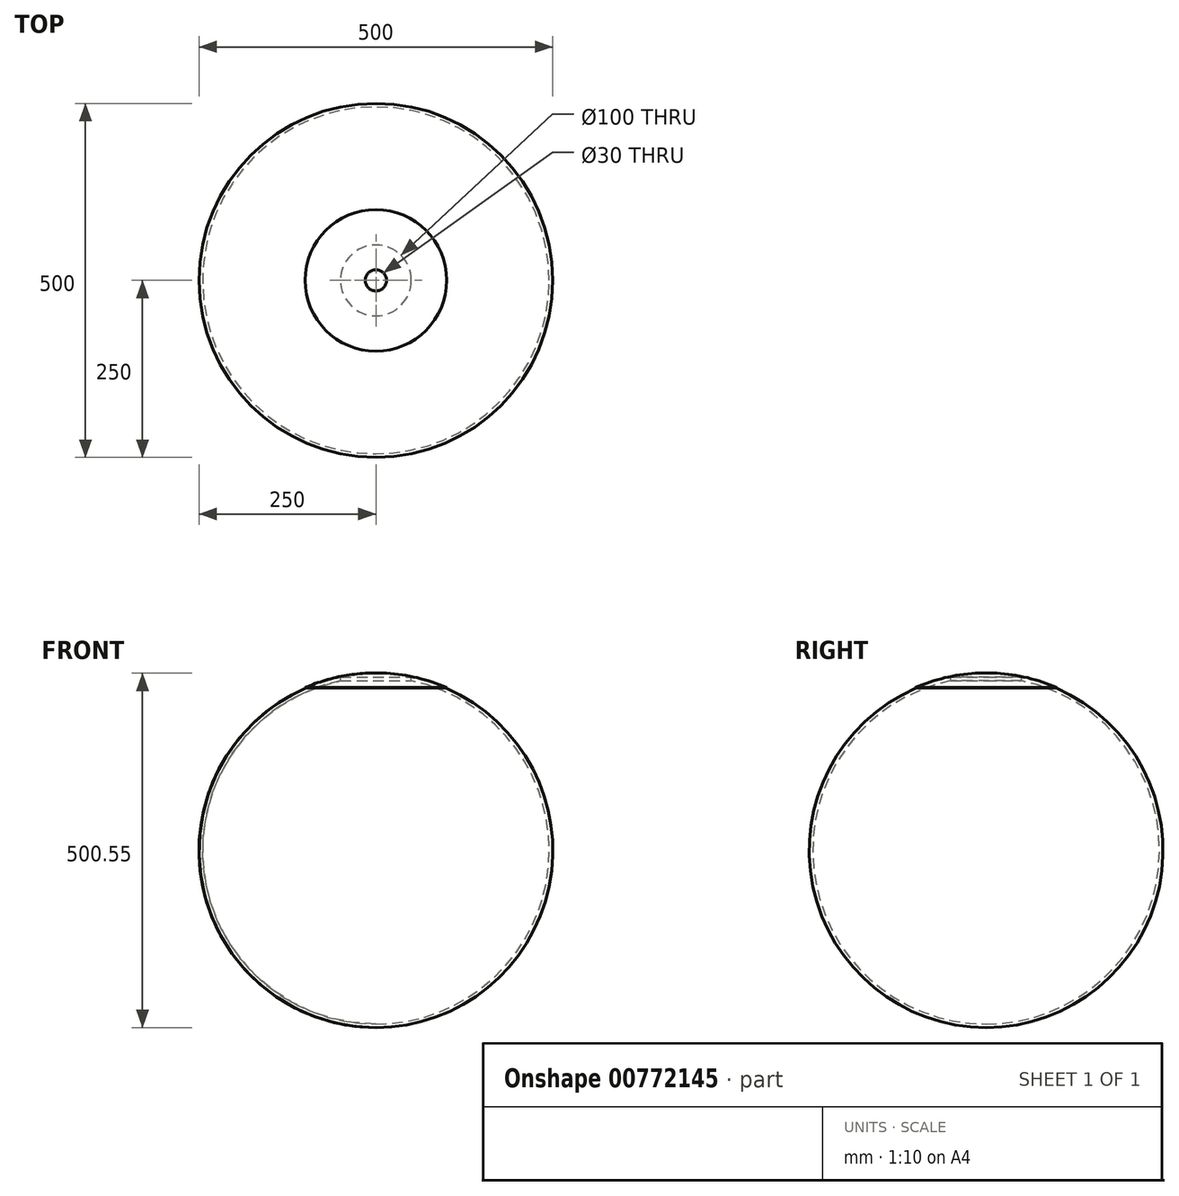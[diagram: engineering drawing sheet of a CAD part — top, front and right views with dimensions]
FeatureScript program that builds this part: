
annotation { "Feature Type Name" : "Feature", "Feature Type Description" : "" }
export const myFeature = defineFeature(function(context is Context, id is Id, definition is map)
    precondition{}
    {
        {
            var Q0;
            Q0=qCreatedBy(makeId("Front.planeOp"),FACE);
            var sketch = newSketch(context, id + "F0", { "sketchPlane" : qUnion([Q0])});
            skArc(sketch, "E0", {"start": v(0, -250) * mm, "mid": v(250, 0) * mm, "end": v(0, 250) * mm});
            skLineSegment(sketch, "E1", {"start": v(0, 269.53) * mm, "end": v(0, 245) * mm});
            skArc(sketch, "E2", {"start": v(0, -245) * mm, "mid": v(245, 0) * mm, "end": v(0, 245) * mm});
            skLineSegment(sketch, "E3.trimOffspring", {"start": v(0, -245) * mm, "end": v(0, -273.85) * mm});
            skSolve(sketch);
        }
        {
            var Q0;
            {var subQ0=sQuery(id+"F0.wireOp",EDGE,"E0");Q0=makeQuery(id+"F0.imprint","IMPRINT",FACE,{"disambiguationData":[TD([[makeQuery(id+"F0.imprint","IMPRINT",EDGE,{"derivedFrom":subQ0}),1.0]])]});}
            var Q1;
            Q1=sQuery(id+"F0.wireOp",EDGE,"E1");
            revolve(context, id + "F1", {"surfaceOperationType" : NewSurfaceOperationType.NEW, "entities" : qUnion([Q0]), "axis" : qUnion([Q1]), "revolveType" : RevolveType.FULL});
        }
        {
            var Q0;
            Q0=qCreatedBy(makeId("Top.planeOp"),FACE);
            cPlane(context, id + "F2", {"entities" : qUnion([Q0]), "cplaneType" : CPlaneType.OFFSET, "offset" : 264.16 * mm, "width" : 152.4 * mm, "height" : 152.4 * mm});
        }
        {
            var Q0;
            Q0=qCreatedBy(id+"F2.planeOp",FACE);
            var sketch = newSketch(context, id + "F3", { "sketchPlane" : qUnion([Q0])});
            skCircle(sketch, "E4", {"center": v(0, 0) * mm, "radius": 50 * mm});
            skSolve(sketch);
        }
        {
            var Q0;
            Q0=makeQuery(id+"F3.imprint","IMPRINT",FACE,{"disambiguationData":[TD([[makeQuery(id+"F3.imprint","IMPRINT",EDGE,{"derivedFrom":sQuery(id+"F3.wireOp",EDGE,"E4")}),1.0]])]});
            extrude(context, id + "F4", {"entities" : qUnion([Q0]), "operationType" : NewBodyOperationType.REMOVE, "oppositeDirection" : true, "depth" : 76.2 * mm, "offsetDistance" : 25.4 * mm});
        }
        {
            var Q0;
            Q0=qCreatedBy(makeId("Right.planeOp"),FACE);
            var sketch = newSketch(context, id + "F5", { "sketchPlane" : qUnion([Q0])});
            skLineSegment(sketch, "E5", {"start": v(0, 250.4) * mm, "end": v(0, 282.94) * mm});
            skLineSegment(sketch, "E6", {"start": v(0, 282.94) * mm, "end": v(100, 282.94) * mm});
            skLineSegment(sketch, "E7", {"start": v(100, 230.22) * mm, "end": v(100, 229.57) * mm});
            skArc(sketch, "E8.0", {"start": v(100, 230.22) * mm, "mid": v(51.07, 245.75) * mm, "end": v(0, 251) * mm});
            skArc(sketch, "E9.0", {"start": v(100.16, 229.5) * mm, "mid": v(51.16, 245.12) * mm, "end": v(0, 250.4) * mm});
            skSolve(sketch);
        }
        {
            var Q0;
            {var subQ4=sQuery(id+"F5.wireOp",EDGE,"E7");Q0=makeQuery(id+"F5.imprint","IMPRINT",FACE,{"disambiguationData":[TD([[makeQuery(id+"F5.imprint","IMPRINT",EDGE,{"derivedFrom":subQ4}),-1.0]])]});}
            var Q1;
            Q1=sQuery(id+"F5.wireOp",EDGE,"E5");
            revolve(context, id + "F6", {"operationType" : NewBodyOperationType.ADD, "surfaceOperationType" : NewSurfaceOperationType.NEW, "entities" : qUnion([Q0]), "axis" : qUnion([Q1]), "revolveType" : RevolveType.FULL});
        }
        {
            var Q0;
            Q0=qCreatedBy(makeId("Top.planeOp"),FACE);
            cPlane(context, id + "F7", {"entities" : qUnion([Q0]), "cplaneType" : CPlaneType.OFFSET, "offset" : 316.23 * mm, "width" : 152.4 * mm, "height" : 152.4 * mm});
        }
        {
            var Q0;
            Q0=qCreatedBy(id+"F7.planeOp",FACE);
            var sketch = newSketch(context, id + "F8", { "sketchPlane" : qUnion([Q0])});
            skCircle(sketch, "E10", {"center": v(0, 0) * mm, "radius": 15 * mm});
            skSolve(sketch);
        }
        {
            var Q0;
            Q0=makeQuery(id+"F8.imprint","IMPRINT",FACE,{"disambiguationData":[TD([[makeQuery(id+"F8.imprint","IMPRINT",EDGE,{"derivedFrom":sQuery(id+"F8.wireOp",EDGE,"E10")}),1.0]])]});
            extrude(context, id + "F9", {"entities" : qUnion([Q0]), "operationType" : NewBodyOperationType.REMOVE, "oppositeDirection" : true, "depth" : 114.3 * mm, "offsetDistance" : 25.4 * mm});
        }
    });
